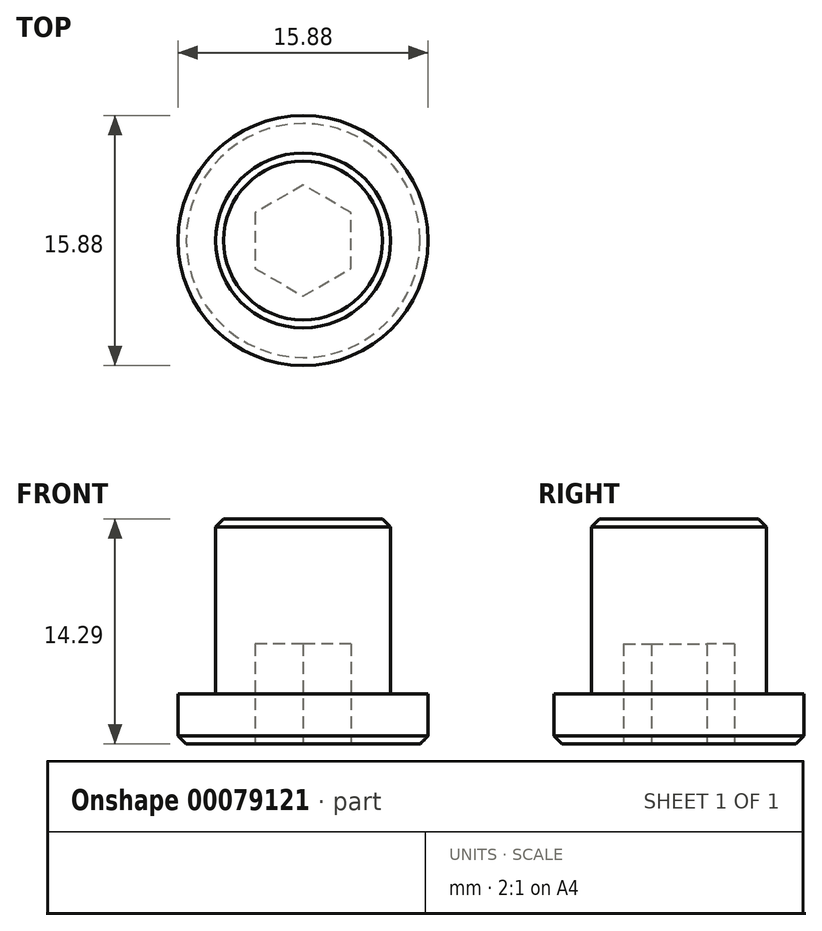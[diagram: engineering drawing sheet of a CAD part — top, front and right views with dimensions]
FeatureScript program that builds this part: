
annotation { "Feature Type Name" : "Feature", "Feature Type Description" : "" }
export const myFeature = defineFeature(function(context is Context, id is Id, definition is map)
    precondition{}
    {
        {
            var Q0;
            Q0=qCreatedBy(makeId("Top.planeOp"),FACE);
            var sketch = newSketch(context, id + "F0", { "sketchPlane" : qUnion([Q0])});
            skCircle(sketch, "E0", {"center": v(0, 0) * mm, "radius": 7.94 * mm});
            skSolve(sketch);
        }
        {
            var Q0;
            Q0 = qSketchRegion(id + "F0", true);
            extrude(context, id + "F1", {"entities" : qUnion([Q0]), "depth" : 3.17 * mm});
        }
        {
            var Q0;
            Q0=makeQuery(id+"F1.opExtrude","CAP_FACE",FACE,{"disambiguationData":[OSD([sQuery(id+"F0.wireOp",EDGE,"E0")])],"isStart":false});
            var sketch = newSketch(context, id + "F2", { "sketchPlane" : qUnion([Q0])});
            skCircle(sketch, "E1", {"center": v(0, 0) * mm, "radius": 5.56 * mm});
            skSolve(sketch);
        }
        {
            var Q0;
            Q0 = qSketchRegion(id + "F2", true);
            extrude(context, id + "F3", {"entities" : qUnion([Q0]), "operationType" : NewBodyOperationType.ADD, "depth" : 11.1 * mm});
        }
        {
            var Q0;
            Q0=makeQuery(id+"F1.opExtrude","CAP_FACE",FACE,{"disambiguationData":[OSD([sQuery(id+"F0.wireOp",EDGE,"E0")])],"isStart":true});
            var sketch = newSketch(context, id + "F4", { "sketchPlane" : qUnion([Q0])});
            skCircle(sketch, "E2.cCircle", {"center": v(0, 0) * mm, "radius": 3.53 * mm, "construction": true});
            skLineSegment(sketch, "E2.0", {"start": v(0, -3.53) * mm, "end": v(-3.06, -1.76) * mm});
            skLineSegment(sketch, "E2.1", {"start": v(-3.06, -1.76) * mm, "end": v(-3.06, 1.76) * mm});
            skLineSegment(sketch, "E2.2", {"start": v(-3.06, 1.76) * mm, "end": v(0, 3.53) * mm});
            skLineSegment(sketch, "E2.3", {"start": v(0, 3.53) * mm, "end": v(3.06, 1.76) * mm});
            skLineSegment(sketch, "E2.4", {"start": v(3.06, 1.76) * mm, "end": v(3.06, -1.76) * mm});
            skLineSegment(sketch, "E2.5", {"start": v(3.06, -1.76) * mm, "end": v(0, -3.53) * mm});
            skSolve(sketch);
        }
        {
            var Q0;
            Q0 = qSketchRegion(id + "F4", true);
            extrude(context, id + "F5", {"entities" : qUnion([Q0]), "operationType" : NewBodyOperationType.REMOVE, "oppositeDirection" : true, "depth" : 6.35 * mm});
        }
        {
            var Q0;
            Q0=makeQuery(id+"F3.opExtrude","CAP_EDGE",EDGE,{"disambiguationData":[OSD([sQuery(id+"F2.wireOp",EDGE,"E1")])],"isStart":false});
            var Q1;
            Q1=makeQuery(id+"F1.opExtrude","CAP_EDGE",EDGE,{"disambiguationData":[OSD([sQuery(id+"F0.wireOp",EDGE,"E0")])],"isStart":true});
            chamfer(context, id + "F6", {"entities" : qUnion([Q0, Q1]), "width" : 0.5 * mm, "tangentPropagation" : true});
        }
    });
